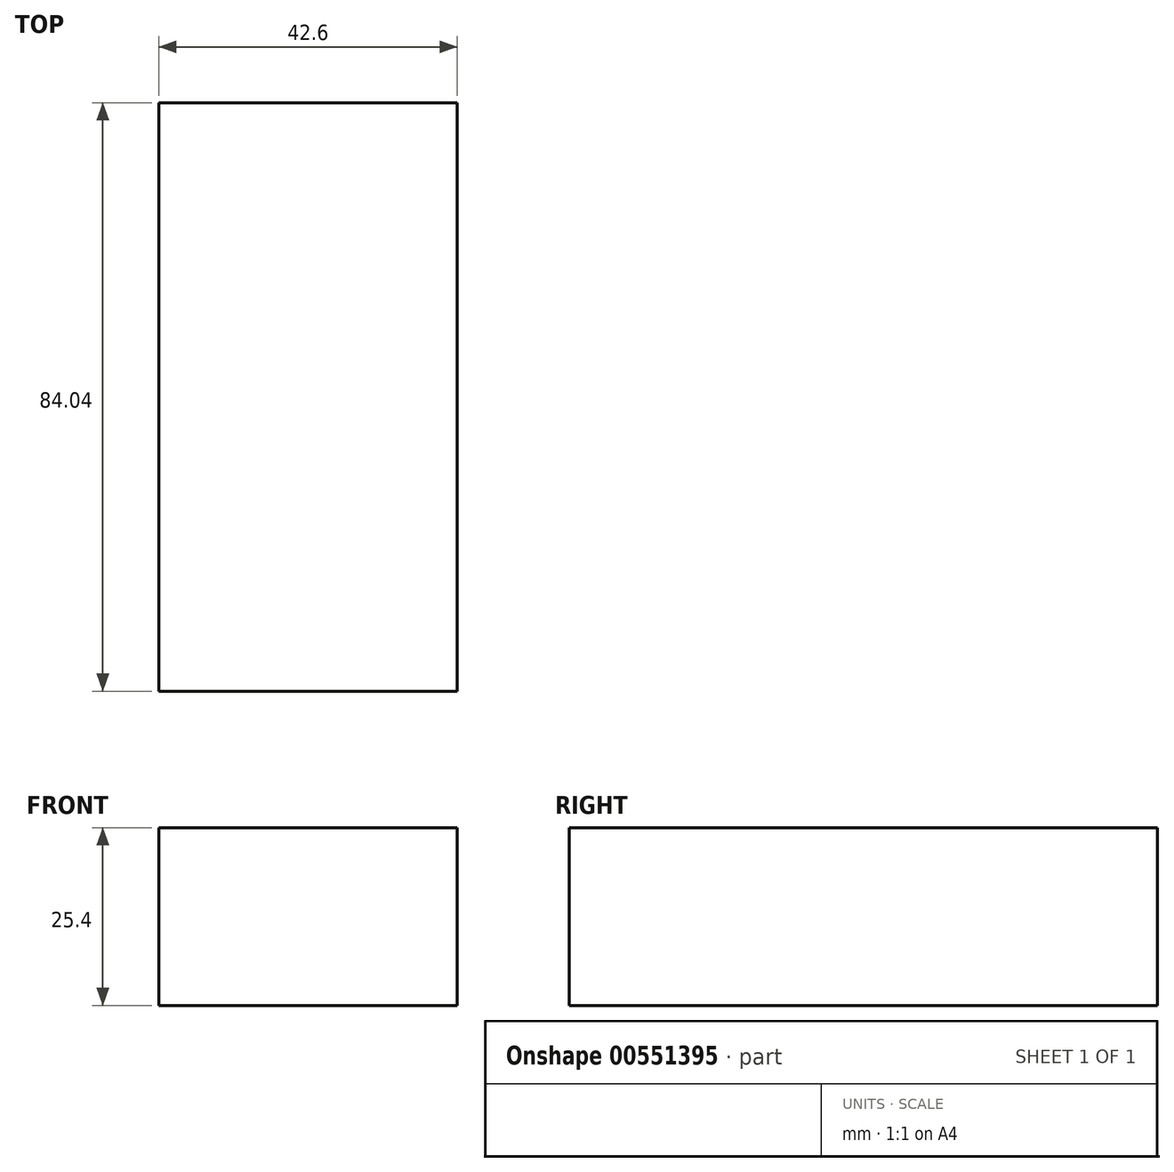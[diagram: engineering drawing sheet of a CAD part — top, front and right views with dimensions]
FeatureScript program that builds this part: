
annotation { "Feature Type Name" : "Feature", "Feature Type Description" : "" }
export const myFeature = defineFeature(function(context is Context, id is Id, definition is map)
    precondition{}
    {
        {
            var Q0;
            Q0=qCreatedBy(makeId("Top.planeOp"),FACE);
            var sketch = newSketch(context, id + "F0", { "sketchPlane" : qUnion([Q0])});
            skLineSegment(sketch, "E0.bottom", {"start": v(21.3, 42.02) * mm, "end": v(-21.3, 42.02) * mm});
            skLineSegment(sketch, "E0.top", {"start": v(21.3, -42.02) * mm, "end": v(-21.3, -42.02) * mm});
            skLineSegment(sketch, "E0.left", {"start": v(21.3, 42.02) * mm, "end": v(21.3, -42.02) * mm});
            skLineSegment(sketch, "E0.right", {"start": v(-21.3, 42.02) * mm, "end": v(-21.3, -42.02) * mm});
            skPoint(sketch, "E0.middle", {"position": v(0, 0) * mm});
            skSolve(sketch);
        }
        {
            var Q0;
            Q0=makeQuery(id+"F0.imprint","IMPRINT",FACE,{"disambiguationData":[TD([[makeQuery(id+"F0.imprint","IMPRINT",EDGE,{"derivedFrom":sQuery(id+"F0.wireOp",EDGE,"E0.bottom")}),1.0]])]});
            extrude(context, id + "F1", {"entities" : qUnion([Q0]), "depth" : 25.4 * mm, "offsetDistance" : 25.4 * mm});
        }
    });
